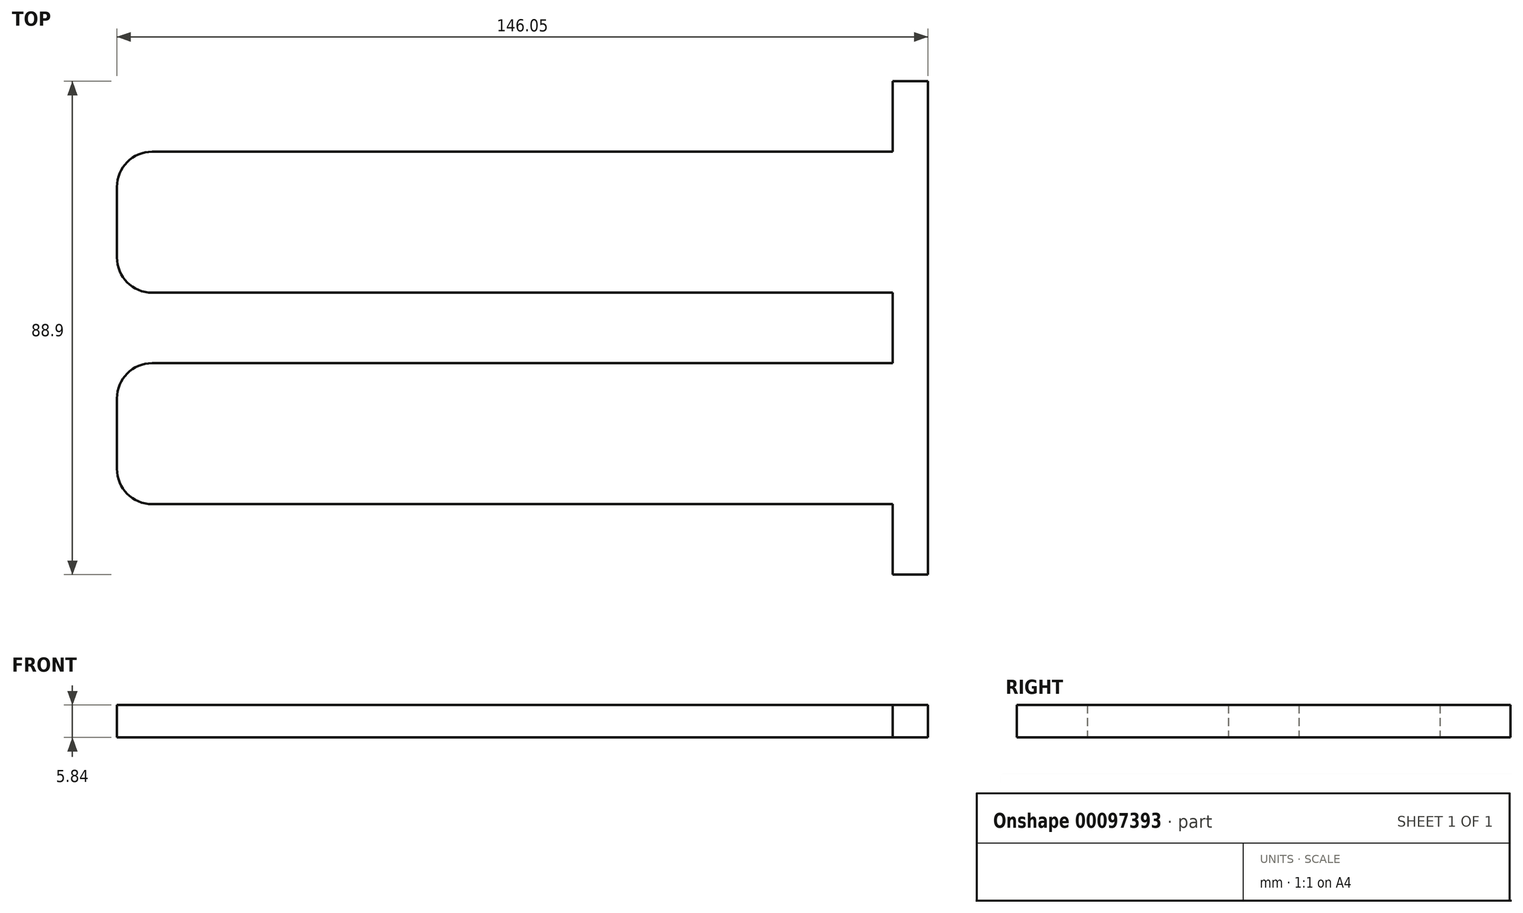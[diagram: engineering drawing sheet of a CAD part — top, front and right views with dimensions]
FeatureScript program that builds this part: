
annotation { "Feature Type Name" : "Feature", "Feature Type Description" : "" }
export const myFeature = defineFeature(function(context is Context, id is Id, definition is map)
    precondition{}
    {
        {
            var Q0;
            Q0=qCreatedBy(makeId("Top.planeOp"),FACE);
            var sketch = newSketch(context, id + "F0", { "sketchPlane" : qUnion([Q0])});
            skLineSegment(sketch, "E0", {"start": v(-38.2, 46.8) * mm, "end": v(95.14, 46.8) * mm});
            skLineSegment(sketch, "E1", {"start": v(95.14, 46.8) * mm, "end": v(95.14, 59.5) * mm});
            skLineSegment(sketch, "E2", {"start": v(95.14, 59.5) * mm, "end": v(101.5, 59.5) * mm});
            skLineSegment(sketch, "E3", {"start": v(101.5, 59.5) * mm, "end": v(101.5, -29.4) * mm});
            skLineSegment(sketch, "E4", {"start": v(101.5, -29.4) * mm, "end": v(95.14, -29.4) * mm});
            skLineSegment(sketch, "E5", {"start": v(95.14, -29.4) * mm, "end": v(95.14, -16.7) * mm});
            skLineSegment(sketch, "E6", {"start": v(95.14, -16.7) * mm, "end": v(-38.2, -16.7) * mm});
            skLineSegment(sketch, "E7", {"start": v(-44.56, -10.35) * mm, "end": v(-44.56, 2.35) * mm});
            skLineSegment(sketch, "E8", {"start": v(-38.2, 8.7) * mm, "end": v(95.14, 8.7) * mm});
            skLineSegment(sketch, "E9", {"start": v(95.14, 8.7) * mm, "end": v(95.14, 21.4) * mm});
            skLineSegment(sketch, "E10", {"start": v(95.14, 21.4) * mm, "end": v(-38.2, 21.4) * mm});
            skLineSegment(sketch, "E11", {"start": v(-44.56, 27.75) * mm, "end": v(-44.56, 40.45) * mm});
            skPoint(sketch, "E12.visualSharp", {"position": v(-44.56, -16.7) * mm});
            skArc(sketch, "E12.filletArc", {"start": v(-44.56, -10.35) * mm, "mid": v(-42.7, -14.84) * mm, "end": v(-38.2, -16.7) * mm});
            skPoint(sketch, "E13.visualSharp", {"position": v(-44.56, 8.7) * mm});
            skArc(sketch, "E13.filletArc", {"start": v(-38.2, 8.7) * mm, "mid": v(-42.7, 6.84) * mm, "end": v(-44.56, 2.35) * mm});
            skPoint(sketch, "E14.visualSharp", {"position": v(-44.56, 21.4) * mm});
            skArc(sketch, "E14.filletArc", {"start": v(-44.56, 27.75) * mm, "mid": v(-42.7, 23.26) * mm, "end": v(-38.2, 21.4) * mm});
            skPoint(sketch, "E15.visualSharp", {"position": v(-44.56, 46.8) * mm});
            skArc(sketch, "E15.filletArc", {"start": v(-38.2, 46.8) * mm, "mid": v(-42.7, 44.94) * mm, "end": v(-44.56, 40.45) * mm});
            skSolve(sketch);
        }
        {
            var Q0;
            Q0=makeQuery(id+"F0.imprint","IMPRINT",FACE,{"disambiguationData":[TD([[makeQuery(id+"F0.imprint","IMPRINT",EDGE,{"derivedFrom":sQuery(id+"F0.wireOp",EDGE,"E0")}),-1.0]])]});
            extrude(context, id + "F1", {"entities" : qUnion([Q0]), "depth" : 5.84 * mm});
        }
    });
